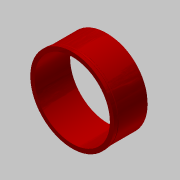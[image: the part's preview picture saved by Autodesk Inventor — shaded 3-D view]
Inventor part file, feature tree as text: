
AUTODESK INVENTOR PART (.ipt)
format: ipt  version: 2017.3 (Build 213257000, 257)  size: 234,496 bytes
history: native  units: in
note: dims shown in document units (in); Inventor stores cm internally (conversion verified against a paired STEP export)
features: extrude x4, sketch x4, chamfer x3, fillet x1, revolve x1
ambient origin geometry x8: Origin, YZ Plane, XZ Plane, XY Plane, X Axis, Y Axis, Z Axis, Center Point
bodies: Solid1 (feature_tree)
feature tree (13):
  extrude  "Extrusion1"  Depth=29.0in
  sketch  "Sketch2"  dims[d2=12.0in d3=0.0in d4=29.23in]
  extrude  "Extrusion2"  Depth=12.0in
  extrude  "Extrusion3"  Depth=1.0in TaperAngle=0.0deg
  chamfer  "Chamfer1"  Distance=1.0in
  extrude  "Extrusion4"  Depth=0.1875in TaperAngle=45.0deg
  fillet  "Fillet1"  Radius=27.98in
  chamfer  "Chamfer2"  Distance=0.5in
  chamfer  "Chamfer3"  Distance=0.0312in
  revolve  "Revolution1"  Angle=45.0deg
  sketch  "Sketch1"  dims[d0=26.5in d1=29.0in]
  sketch  "Sketch3"  dims[d5=29.48in d6=2.0in d7=0.0in d8=1.0in d9=0.0in]
  sketch  "Sketch4"  dims[d10=0.115in d11=0.125in d12=45.0deg d13=27.98in d14=0.5in d15=0.0in d16=0.0312in d17=0.0312in d18=0.125in d19=45.0deg d20=0.0312in d21=0.125in d22=45.0deg d23=0.4375in d24=0.125in d25=0.1875in d26=1.25in d27=45.0deg d28=90.0deg]
